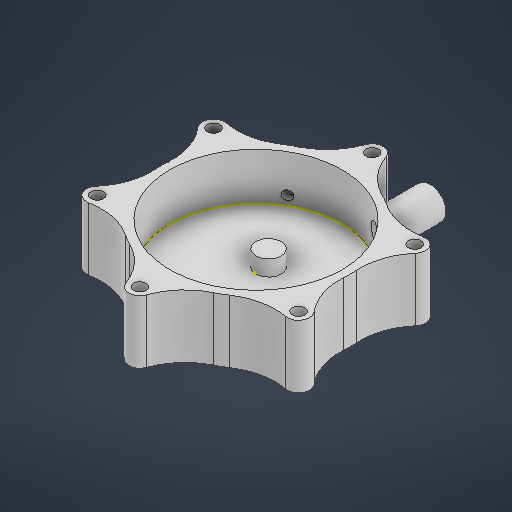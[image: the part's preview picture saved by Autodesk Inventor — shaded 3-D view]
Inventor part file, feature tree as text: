
AUTODESK INVENTOR PART (.ipt)
format: ipt  version: 2025.3 (Build 293356000, 356)  size: 323,072 bytes
history: native  units: mm
features: sketch x6, extrude x6, plane x2
ambient origin geometry x8: Origin, YZ Plane, XZ Plane, XY Plane, X Axis, Y Axis, Z Axis, Center Point
bodies: Body1 (feature_tree)
feature tree (14):
  sketch  "Sketch1"  dims[d16=60.0mm d17=55.0mm]
  extrude  "Extrusion5"  Depth=55.0mm
  extrude  "Extrusion6"  Depth=37.0mm
  sketch  "Sketch4"  dims[d21=20.0mm d22=4.0mm]
  plane  "Work Plane3"
  sketch  "Sketch5"  dims[d23=60.0mm d25=360.0deg d27=20.0mm d28=0.0mm]
  extrude  "Extrusion7"  Depth=4.0mm
  extrude  "Extrusion8"  Depth=20.0mm TaperAngle=0.0deg
  plane  "Work Plane4"
  extrude  "Extrusion9"  Depth=10.0mm
  extrude  "Extrusion11"  Depth=4.0mm
  sketch  "Sketch Circular Pattern1"  dims[d18=7.0mm d19=37.0mm]
  sketch  "Sketch6"  dims[d29=5.0mm d30=0.0mm d33=10.0mm]
  sketch  "Sketch8"  dims[d34=6.0mm d35=8.0mm d36=15.0mm d37=3.0mm d38=0.0mm d39=10.0mm d40=0.0mm d41=3.0mm d42=3.0mm d43=8.0mm d44=10.0mm d45=0.0mm d53=5.0mm d54=0.0mm d57=8.0mm d58=45.0mm d59=4.0mm d3=0.5mm d4=0.872665mm d5=0.5mm d6=0.872665mm d60=0.5mm d61=0.872665mm d62=0.5mm d63=0.872665mm]
